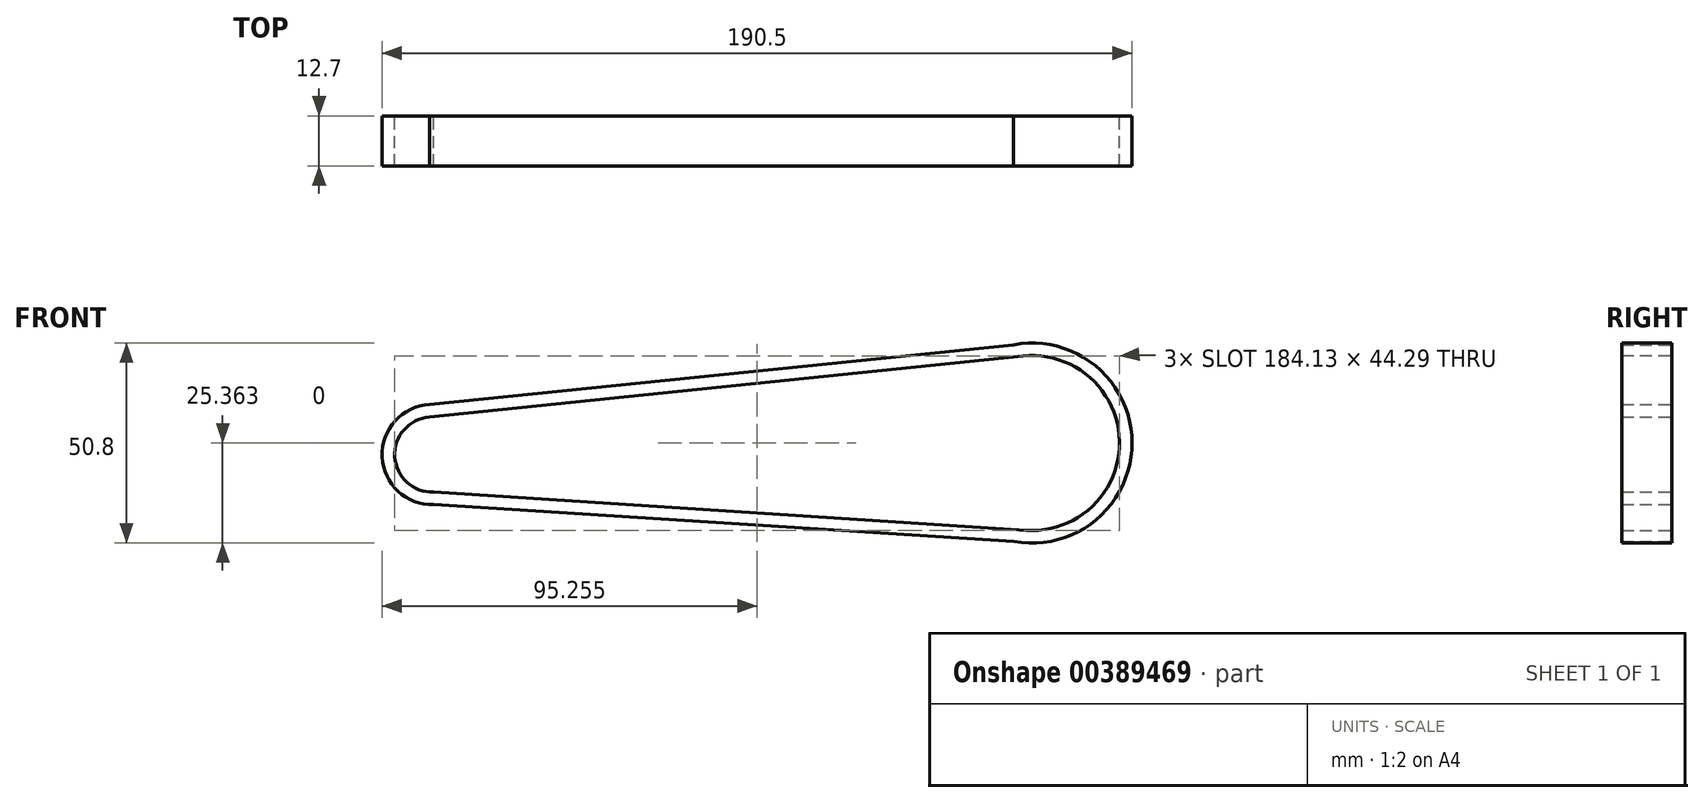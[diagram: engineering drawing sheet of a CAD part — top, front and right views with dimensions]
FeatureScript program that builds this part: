
annotation { "Feature Type Name" : "Feature", "Feature Type Description" : "" }
export const myFeature = defineFeature(function(context is Context, id is Id, definition is map)
    precondition{}
    {
        {
            var Q0;
            Q0=qCreatedBy(makeId("Front.planeOp"),FACE);
            var sketch = newSketch(context, id + "F0", { "sketchPlane" : qUnion([Q0])});
            skArc(sketch, "E0", {"start": v(47.85, -17.94) * mm, "mid": v(77.78, 7.14) * mm, "end": v(47.67, 32) * mm});
            skArc(sketch, "E1", {"start": v(-100.7, 16.78) * mm, "mid": v(-112.7, 3.56) * mm, "end": v(-99.61, -8.6) * mm});
            skLineSegment(sketch, "E2", {"start": v(-100.7, 16.78) * mm, "end": v(47.67, 32) * mm});
            skLineSegment(sketch, "E3", {"start": v(-99.61, -8.6) * mm, "end": v(47.85, -17.94) * mm});
            skArc(sketch, "E4", {"start": v(-100.7, 13.6) * mm, "mid": v(-109.53, 3.56) * mm, "end": v(-99.61, -5.41) * mm});
            skArc(sketch, "E5", {"start": v(50.95, -15.13) * mm, "mid": v(74.6, 7.47) * mm, "end": v(50.1, 29.16) * mm});
            skLineSegment(sketch, "E6", {"start": v(-100.7, 13.6) * mm, "end": v(50.1, 29.16) * mm});
            skLineSegment(sketch, "E7", {"start": v(-99.61, -5.41) * mm, "end": v(50.95, -15.13) * mm});
            skSolve(sketch);
        }
        {
            var Q0;
            Q0 = qSketchRegion(id + "F0", true);
            extrude(context, id + "F1", {"entities" : qUnion([Q0]), "depth" : 12.7 * mm});
        }
    });
